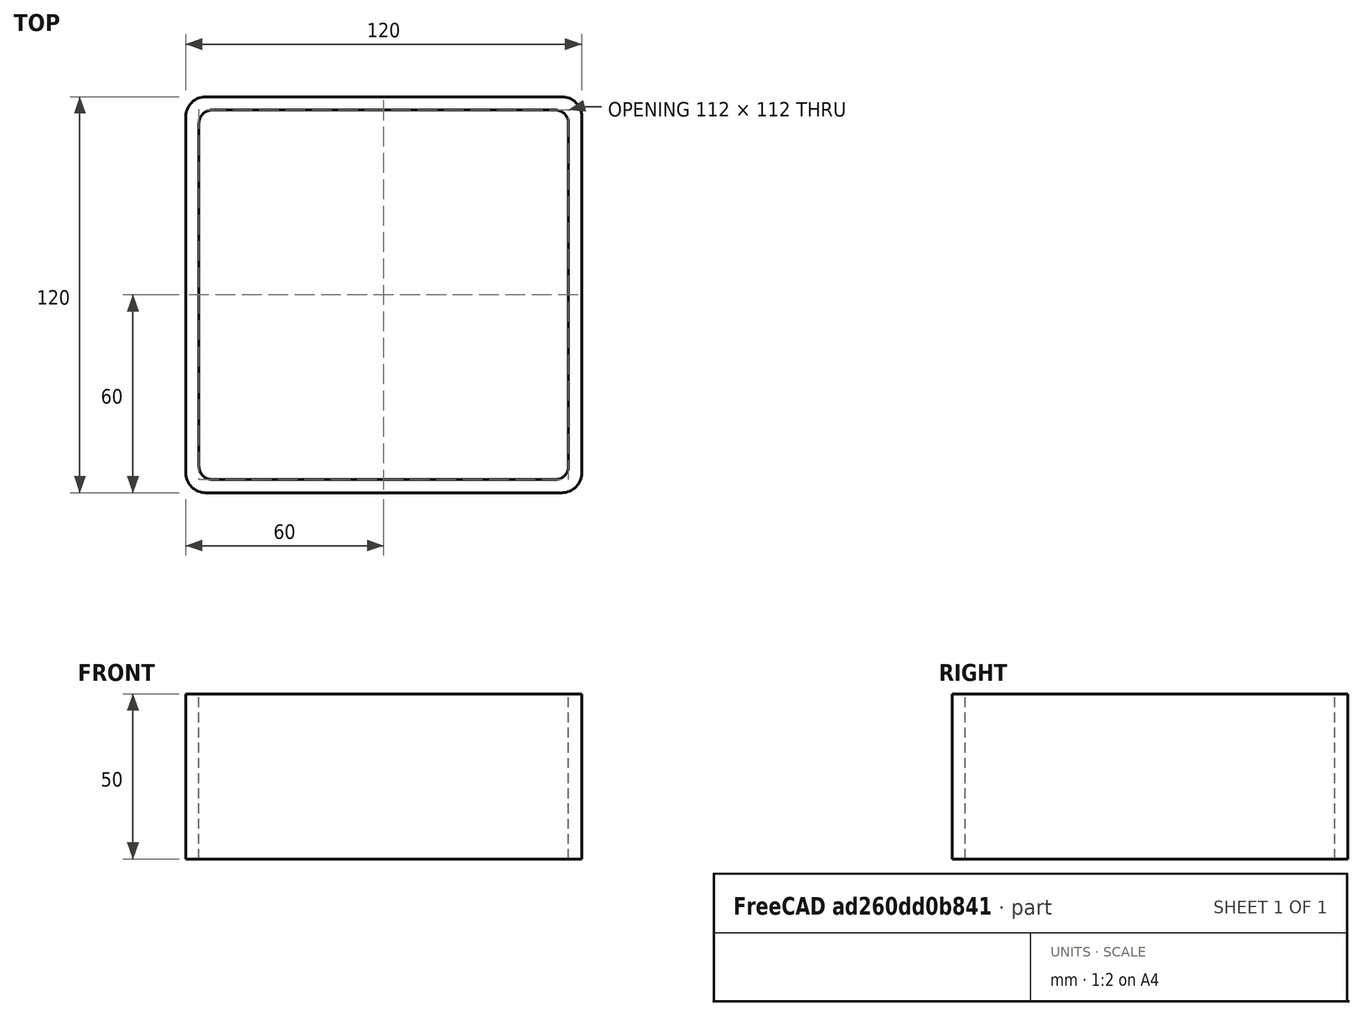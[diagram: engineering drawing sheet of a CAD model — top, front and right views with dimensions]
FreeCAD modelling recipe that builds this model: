
FCSTD DOCUMENT  (FreeCAD 0.15R4671 (Git))
Label: Square hollow section 120x120x4 EN10219 S235JRH
License: All rights reserved
LicenseURL: http://en.wikipedia.org/wiki/All_rights_reserved
objects: Sketcher::SketchObject×1, Part::Extrusion×1
note: 2 computed .brp shape members not serialized (recipe doc carries the construction recipe); baked Part::Feature solids carry a one-line shape summary decoded from their .brp

FEATURE [Sketcher::SketchObject] Sketch
  sketch-geometry (16):
    g0: LineSegment StartX=-52 StartY=56 StartZ=0 EndX=52 EndY=56 EndZ=0
    g1: LineSegment StartX=56 StartY=52 StartZ=0 EndX=56 EndY=-52 EndZ=0
    g2: LineSegment StartX=52 StartY=-56 StartZ=0 EndX=-52 EndY=-56 EndZ=0
    g3: LineSegment StartX=-56 StartY=-52 StartZ=0 EndX=-56 EndY=52 EndZ=0
    g4: LineSegment StartX=-54 StartY=60 StartZ=0 EndX=54 EndY=60 EndZ=0
    g5: LineSegment StartX=60 StartY=54 StartZ=0 EndX=60 EndY=-54 EndZ=0
    g6: LineSegment StartX=54 StartY=-60 StartZ=0 EndX=-54 EndY=-60 EndZ=0
    g7: LineSegment StartX=-60 StartY=-54 StartZ=0 EndX=-60 EndY=54 EndZ=0
    g8: ArcOfCircle CenterX=-52 CenterY=52 CenterZ=0 NormalX=0 NormalY=0 NormalZ=1 Radius=4 StartAngle=1.5708 EndAngle=3.14159
    g9: ArcOfCircle CenterX=52 CenterY=52 CenterZ=0 NormalX=0 NormalY=0 NormalZ=1 Radius=4 StartAngle=0 EndAngle=1.5708
    g10: ArcOfCircle CenterX=52 CenterY=-52 CenterZ=0 NormalX=0 NormalY=0 NormalZ=1 Radius=4 StartAngle=4.71239 EndAngle=6.28319
    g11: ArcOfCircle CenterX=-52 CenterY=-52 CenterZ=0 NormalX=0 NormalY=0 NormalZ=1 Radius=4 StartAngle=3.14159 EndAngle=4.71239
    g12: ArcOfCircle CenterX=54 CenterY=54 CenterZ=0 NormalX=0 NormalY=0 NormalZ=1 Radius=6 StartAngle=0 EndAngle=1.5708
    g13: ArcOfCircle CenterX=54 CenterY=-54 CenterZ=0 NormalX=0 NormalY=0 NormalZ=1 Radius=6 StartAngle=4.71239 EndAngle=6.28319
    g14: ArcOfCircle CenterX=-54 CenterY=-54 CenterZ=0 NormalX=0 NormalY=0 NormalZ=1 Radius=6 StartAngle=3.14159 EndAngle=4.71239
    g15: ArcOfCircle CenterX=-54 CenterY=54 CenterZ=0 NormalX=0 NormalY=0 NormalZ=1 Radius=6 StartAngle=1.5708 EndAngle=3.14159
  constraints (36):
    c: Horizontal(g2)
    c: Vertical(g3)
    c: Horizontal(g6)
    c: Vertical(g7)
    c: Tangent(g3,g8) = 1.5708
    c: Tangent(g0,g8) = 1.5708
    c: Tangent(g0,g9) = 1.5708
    c: Tangent(g1,g9) = 1.5708
    c: Tangent(g1,g10) = 1.5708
    c: Tangent(g2,g10) = 1.5708
    c: Tangent(g2,g11) = 1.5708
    c: Tangent(g3,g11) = 1.5708
    c: Tangent(g4,g12) = 1.5708
    c: Tangent(g5,g12) = 1.5708
    c: Tangent(g5,g13) = 1.5708
    c: Tangent(g6,g13) = 1.5708
    c: Tangent(g6,g14) = 1.5708
    c: Tangent(g7,g14) = 1.5708
    c: Tangent(g7,g15) = 1.5708
    c: Tangent(g4,g15) = 1.5708
    c: Equal(g9,g8)
    c: Equal(g9,g11)
    c: Equal(g9,g10)
    c: Equal(g12,g15)
    c: Equal(g12,g14)
    c: Equal(g12,g13)
    c: Symmetric(g4,g6,g-1)
    c: Symmetric(g7,g5,g-2)
    c: DistanceY(g4,g6) = -120
    c: DistanceX(g7,g5) = 120
    c: Symmetric(g3,g1,g-2)
    c: Symmetric(g0,g2,g-1)
    c: DistanceY(g0,g4) = 4
    c: DistanceX(g5,g1) = -4
    c: Radius(g9) = 4
    c: Radius(g12) = 6
FEATURE [Part::Extrusion] Extrude  label="Square hollow section 120x120x4 EN10219 S235JRH"
  Base = -> Sketch
  Dir = (0,0,50)
  Solid = true
